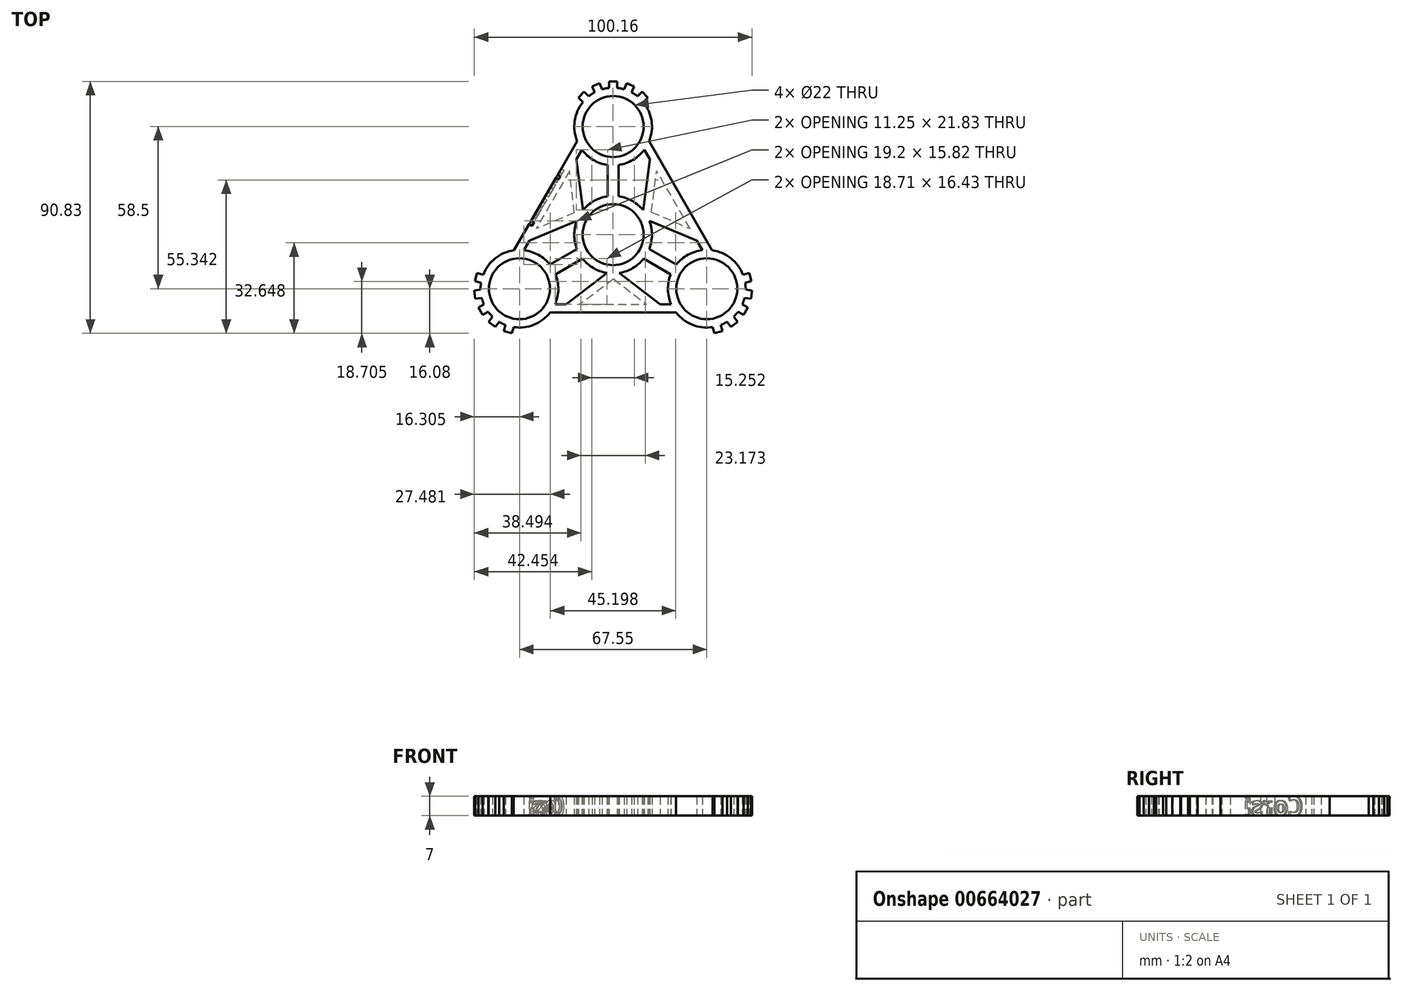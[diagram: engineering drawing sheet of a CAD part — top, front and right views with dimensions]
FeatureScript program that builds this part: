
annotation { "Feature Type Name" : "Feature", "Feature Type Description" : "" }
export const myFeature = defineFeature(function(context is Context, id is Id, definition is map)
    precondition{}
    {
        {
            var Q0;
            Q0=qCreatedBy(makeId("Top.planeOp"),FACE);
            var sketch = newSketch(context, id + "F0", { "sketchPlane" : qUnion([Q0])});
            skCircle(sketch, "E0", {"center": v(0, 0) * mm, "radius": 11 * mm});
            skArc(sketch, "E1.0", {"start": v(-2, 13.86) * mm, "mid": v(-6.9, 12.18) * mm, "end": v(-10.85, 8.84) * mm});
            skCircle(sketch, "E2", {"center": v(0, 39) * mm, "radius": 11 * mm});
            skArc(sketch, "E3.0", {"start": v(-10.9, 47.78) * mm, "mid": v(-13.85, 41.03) * mm, "end": v(-12.97, 33.72) * mm});
            skLineSegment(sketch, "E4", {"start": v(0, 11) * mm, "end": v(0, 28) * mm, "construction": true});
            skLineSegment(sketch, "E5.0", {"start": v(2, 13.86) * mm, "end": v(2, 25.14) * mm});
            skLineSegment(sketch, "E6.0", {"start": v(-2, 13.86) * mm, "end": v(-2, 25.14) * mm});
            skLineSegment(sketch, "E7", {"start": v(0, 53) * mm, "end": v(0, 55) * mm, "construction": true});
            skLineSegment(sketch, "E8.0", {"start": v(1.5, 52.92) * mm, "end": v(1.5, 55.25) * mm});
            skLineSegment(sketch, "E9.0", {"start": v(-1.5, 52.92) * mm, "end": v(-1.5, 55.25) * mm});
            skLineSegment(sketch, "E10", {"start": v(-1.5, 55.25) * mm, "end": v(1.5, 55.25) * mm});
            skLineSegment(sketch, "E11.1.0", {"start": v(4.83, 54.59) * mm, "end": v(7.6, 53.44) * mm});
            skLineSegment(sketch, "E11.1.1", {"start": v(3.94, 52.43) * mm, "end": v(4.83, 54.59) * mm});
            skLineSegment(sketch, "E11.1.2", {"start": v(6.71, 51.29) * mm, "end": v(7.6, 53.44) * mm});
            skLineSegment(sketch, "E11.2.0", {"start": v(10.43, 51.55) * mm, "end": v(12.55, 49.43) * mm});
            skLineSegment(sketch, "E11.2.1", {"start": v(8.78, 49.9) * mm, "end": v(10.43, 51.55) * mm});
            skLineSegment(sketch, "E11.2.2", {"start": v(10.9, 47.78) * mm, "end": v(12.55, 49.43) * mm});
            skLineSegment(sketch, "E11.anchor1", {"start": v(0, 39) * mm, "end": v(-1.5, 55.25) * mm, "construction": true});
            skLineSegment(sketch, "E11.anchor2", {"start": v(0, 39) * mm, "end": v(10.43, 51.55) * mm, "construction": true});
            skLineSegment(sketch, "E12.MirrorCS", {"start": v(-4.83, 54.59) * mm, "end": v(-7.6, 53.44) * mm});
            skLineSegment(sketch, "E13.MirrorCS", {"start": v(-3.94, 52.43) * mm, "end": v(-4.83, 54.59) * mm});
            skLineSegment(sketch, "E14.MirrorCS", {"start": v(-6.71, 51.29) * mm, "end": v(-7.6, 53.44) * mm});
            skLineSegment(sketch, "E15.MirrorCS", {"start": v(-8.78, 49.9) * mm, "end": v(-10.43, 51.55) * mm});
            skLineSegment(sketch, "E16.MirrorCS", {"start": v(-10.43, 51.55) * mm, "end": v(-12.55, 49.43) * mm});
            skLineSegment(sketch, "E17.MirrorCS", {"start": v(-10.9, 47.78) * mm, "end": v(-12.55, 49.43) * mm});
            skArc(sketch, "E18.trimOffspring", {"start": v(-6.71, 51.29) * mm, "mid": v(-7.78, 50.64) * mm, "end": v(-8.78, 49.9) * mm});
            skArc(sketch, "E19.trimOffspring", {"start": v(-1.29, 52.94) * mm, "mid": v(-2.63, 52.75) * mm, "end": v(-3.94, 52.43) * mm});
            skArc(sketch, "E20.trimOffspring", {"start": v(3.94, 52.43) * mm, "mid": v(2.73, 52.73) * mm, "end": v(1.5, 52.92) * mm});
            skArc(sketch, "E21.trimOffspring", {"start": v(8.95, 49.77) * mm, "mid": v(7.87, 50.58) * mm, "end": v(6.71, 51.29) * mm});
            skArc(sketch, "E22.trimOffspring", {"start": v(2, 25.14) * mm, "mid": v(7.18, 26.98) * mm, "end": v(11.26, 30.68) * mm});
            skLineSegment(sketch, "E23.1.0", {"start": v(-33.77, -19.5) * mm, "end": v(-47.1, -28.92) * mm, "construction": true});
            skPoint(sketch, "E23.1.1", {"position": v(-33.77, -19.5) * mm});
            skCircle(sketch, "E23.1.2", {"center": v(-33.77, -19.5) * mm, "radius": 11 * mm});
            skLineSegment(sketch, "E23.1.3", {"start": v(-9.53, -5.5) * mm, "end": v(-24.25, -14) * mm, "construction": true});
            skArc(sketch, "E23.1.4", {"start": v(-35.93, -33.33) * mm, "mid": v(-28.6, -32.51) * mm, "end": v(-22.72, -28.09) * mm});
            skLineSegment(sketch, "E23.1.5", {"start": v(-13, -5.2) * mm, "end": v(-22.77, -10.84) * mm});
            skLineSegment(sketch, "E23.1.6", {"start": v(-11, -8.66) * mm, "end": v(-20.77, -14.3) * mm});
            skLineSegment(sketch, "E23.1.7", {"start": v(-33.77, -19.5) * mm, "end": v(-49.86, -16.74) * mm, "construction": true});
            skArc(sketch, "E23.1.8", {"start": v(-22.77, -10.84) * mm, "mid": v(-26.96, -7.27) * mm, "end": v(-32.2, -5.59) * mm});
            skLineSegment(sketch, "E23.1.9", {"start": v(-41.06, -31.46) * mm, "end": v(-42.48, -33.3) * mm});
            skLineSegment(sketch, "E23.1.10", {"start": v(-35.93, -33.33) * mm, "end": v(-36.53, -35.58) * mm});
            skLineSegment(sketch, "E23.1.11", {"start": v(-49.86, -16.74) * mm, "end": v(-49.08, -13.85) * mm});
            skLineSegment(sketch, "E23.1.12", {"start": v(-47.77, -19.83) * mm, "end": v(-50.08, -20.13) * mm});
            skArc(sketch, "E23.1.13", {"start": v(-47.57, -17.13) * mm, "mid": v(-47.74, -18.48) * mm, "end": v(-47.77, -19.83) * mm});
            skLineSegment(sketch, "E23.1.14", {"start": v(-44.86, -31.48) * mm, "end": v(-42.48, -33.3) * mm});
            skLineSegment(sketch, "E23.1.15", {"start": v(-45.9, -26.5) * mm, "end": v(-47.63, -27.5) * mm, "construction": true});
            skLineSegment(sketch, "E23.1.16", {"start": v(-46.58, -25.16) * mm, "end": v(-48.6, -26.33) * mm});
            skLineSegment(sketch, "E23.1.17", {"start": v(-47.1, -28.92) * mm, "end": v(-48.6, -26.33) * mm});
            skLineSegment(sketch, "E23.1.18", {"start": v(-45.08, -27.76) * mm, "end": v(-47.1, -28.92) * mm});
            skLineSegment(sketch, "E23.1.19", {"start": v(-49.7, -23.1) * mm, "end": v(-50.08, -20.13) * mm});
            skLineSegment(sketch, "E23.1.20", {"start": v(-47.38, -22.8) * mm, "end": v(-49.7, -23.1) * mm});
            skArc(sketch, "E23.1.21", {"start": v(-47.38, -22.8) * mm, "mid": v(-47.03, -24) * mm, "end": v(-46.58, -25.16) * mm});
            skArc(sketch, "E23.1.22", {"start": v(-41.06, -31.46) * mm, "mid": v(-39.97, -32.06) * mm, "end": v(-38.83, -32.56) * mm});
            skLineSegment(sketch, "E23.1.23", {"start": v(-39.43, -34.8) * mm, "end": v(-36.53, -35.58) * mm});
            skLineSegment(sketch, "E23.1.24", {"start": v(-43.44, -29.63) * mm, "end": v(-44.86, -31.48) * mm});
            skLineSegment(sketch, "E23.1.25", {"start": v(-46.83, -14.45) * mm, "end": v(-49.08, -13.85) * mm});
            skArc(sketch, "E23.1.26", {"start": v(-45.2, -27.58) * mm, "mid": v(-44.37, -28.65) * mm, "end": v(-43.44, -29.63) * mm});
            skLineSegment(sketch, "E23.1.27", {"start": v(-38.83, -32.56) * mm, "end": v(-39.43, -34.8) * mm});
            skLineSegment(sketch, "E23.1.28", {"start": v(-47.6, -17.35) * mm, "end": v(-49.86, -16.74) * mm});
            skLineSegment(sketch, "E23.2.0", {"start": v(33.77, -19.5) * mm, "end": v(48.6, -26.33) * mm, "construction": true});
            skPoint(sketch, "E23.2.1", {"position": v(33.77, -19.5) * mm});
            skCircle(sketch, "E23.2.2", {"center": v(33.77, -19.5) * mm, "radius": 11 * mm});
            skLineSegment(sketch, "E23.2.3", {"start": v(9.53, -5.5) * mm, "end": v(24.25, -14) * mm, "construction": true});
            skArc(sketch, "E23.2.4", {"start": v(46.83, -14.45) * mm, "mid": v(42.46, -8.52) * mm, "end": v(35.69, -5.63) * mm});
            skLineSegment(sketch, "E23.2.5", {"start": v(11, -8.66) * mm, "end": v(20.77, -14.3) * mm});
            skLineSegment(sketch, "E23.2.6", {"start": v(13, -5.2) * mm, "end": v(22.77, -10.84) * mm});
            skLineSegment(sketch, "E23.2.7", {"start": v(33.77, -19.5) * mm, "end": v(39.43, -34.8) * mm, "construction": true});
            skArc(sketch, "E23.2.8", {"start": v(20.77, -14.3) * mm, "mid": v(19.78, -19.71) * mm, "end": v(20.94, -25.09) * mm});
            skLineSegment(sketch, "E23.2.9", {"start": v(47.77, -19.83) * mm, "end": v(50.08, -20.13) * mm});
            skLineSegment(sketch, "E23.2.10", {"start": v(46.83, -14.45) * mm, "end": v(49.08, -13.85) * mm});
            skLineSegment(sketch, "E23.2.11", {"start": v(39.43, -34.8) * mm, "end": v(36.53, -35.58) * mm});
            skLineSegment(sketch, "E23.2.12", {"start": v(41.06, -31.46) * mm, "end": v(42.48, -33.3) * mm});
            skArc(sketch, "E23.2.13", {"start": v(38.63, -32.63) * mm, "mid": v(39.87, -32.1) * mm, "end": v(41.06, -31.46) * mm});
            skLineSegment(sketch, "E23.2.14", {"start": v(49.7, -23.1) * mm, "end": v(50.08, -20.13) * mm});
            skLineSegment(sketch, "E23.2.15", {"start": v(45.9, -26.5) * mm, "end": v(47.63, -27.5) * mm, "construction": true});
            skLineSegment(sketch, "E23.2.16", {"start": v(45.08, -27.76) * mm, "end": v(47.1, -28.92) * mm});
            skLineSegment(sketch, "E23.2.17", {"start": v(48.6, -26.33) * mm, "end": v(47.1, -28.92) * mm});
            skLineSegment(sketch, "E23.2.18", {"start": v(46.58, -25.16) * mm, "end": v(48.6, -26.33) * mm});
            skLineSegment(sketch, "E23.2.19", {"start": v(44.86, -31.48) * mm, "end": v(42.48, -33.3) * mm});
            skLineSegment(sketch, "E23.2.20", {"start": v(43.44, -29.63) * mm, "end": v(44.86, -31.48) * mm});
            skArc(sketch, "E23.2.21", {"start": v(43.44, -29.63) * mm, "mid": v(44.3, -28.73) * mm, "end": v(45.08, -27.76) * mm});
            skArc(sketch, "E23.2.22", {"start": v(47.77, -19.83) * mm, "mid": v(47.75, -18.58) * mm, "end": v(47.6, -17.35) * mm});
            skLineSegment(sketch, "E23.2.23", {"start": v(49.86, -16.74) * mm, "end": v(49.08, -13.85) * mm});
            skLineSegment(sketch, "E23.2.24", {"start": v(47.38, -22.8) * mm, "end": v(49.7, -23.1) * mm});
            skLineSegment(sketch, "E23.2.25", {"start": v(35.93, -33.33) * mm, "end": v(36.53, -35.58) * mm});
            skArc(sketch, "E23.2.26", {"start": v(46.5, -25.36) * mm, "mid": v(47, -24.1) * mm, "end": v(47.38, -22.8) * mm});
            skLineSegment(sketch, "E23.2.27", {"start": v(47.6, -17.35) * mm, "end": v(49.86, -16.74) * mm});
            skLineSegment(sketch, "E23.2.28", {"start": v(38.83, -32.56) * mm, "end": v(39.43, -34.8) * mm});
            skArc(sketch, "E24.trimOffspring", {"start": v(13, -5.2) * mm, "mid": v(14, -0.12) * mm, "end": v(13.09, 4.98) * mm});
            skArc(sketch, "E25.trimOffspring", {"start": v(-11, -8.66) * mm, "mid": v(-7.1, -12.06) * mm, "end": v(-2.23, -13.82) * mm});
            skLineSegment(sketch, "E26", {"start": v(-12.97, 33.72) * mm, "end": v(-35.69, -5.63) * mm});
            skLineSegment(sketch, "E27.0", {"start": v(-11.26, 30.68) * mm, "end": v(-13.25, 27.23) * mm});
            skArc(sketch, "E28.trimOffspring", {"start": v(-11.26, 30.68) * mm, "mid": v(-7.18, 26.98) * mm, "end": v(-2, 25.14) * mm});
            skArc(sketch, "E29.trimOffspring", {"start": v(-35.69, -5.63) * mm, "mid": v(-42.46, -8.52) * mm, "end": v(-46.83, -14.45) * mm});
            skLineSegment(sketch, "E30", {"start": v(-12.12, 7) * mm, "end": v(-28.97, 0) * mm, "construction": true});
            skLineSegment(sketch, "E31", {"start": v(-12.12, 7) * mm, "end": v(-21.73, 12.54) * mm, "construction": true});
            skLineSegment(sketch, "E32.0", {"start": v(-13.98, 7.85) * mm, "end": v(-27.74, 2.14) * mm});
            skLineSegment(sketch, "E33.0", {"start": v(-13.09, 4.98) * mm, "end": v(-30.2, -2.14) * mm});
            skLineSegment(sketch, "E34.trimOffspring", {"start": v(-30.2, -2.14) * mm, "end": v(-32.2, -5.59) * mm});
            skArc(sketch, "E35.trimOffspring", {"start": v(-13.09, 4.98) * mm, "mid": v(-14, -0.12) * mm, "end": v(-13, -5.2) * mm});
            skLineSegment(sketch, "E36.MirrorCS", {"start": v(-10.85, 8.84) * mm, "end": v(-13.25, 27.23) * mm});
            skLineSegment(sketch, "E37.trimOffspring", {"start": v(-15.72, 22.95) * mm, "end": v(-27.74, 2.14) * mm});
            skPoint(sketch, "E38.orphan", {"position": v(-10.45, 9.32) * mm});
            skLineSegment(sketch, "E39.trimOffspring", {"start": v(-13.98, 7.85) * mm, "end": v(-15.72, 22.95) * mm});
            skPoint(sketch, "E40.MirrorCS.start.orphan", {"position": v(-13.3, 4.38) * mm});
            skLineSegment(sketch, "E41.1.0", {"start": v(-22.72, -28.09) * mm, "end": v(22.72, -28.09) * mm});
            skLineSegment(sketch, "E41.1.1", {"start": v(0.2, -16.04) * mm, "end": v(-12.02, -25.09) * mm});
            skLineSegment(sketch, "E41.1.2", {"start": v(0, -14) * mm, "end": v(0, -25.09) * mm, "construction": true});
            skLineSegment(sketch, "E41.1.3", {"start": v(-12.02, -25.09) * mm, "end": v(12.02, -25.09) * mm});
            skLineSegment(sketch, "E41.1.4", {"start": v(-2.23, -13.82) * mm, "end": v(-16.95, -25.09) * mm});
            skLineSegment(sketch, "E41.1.5", {"start": v(16.95, -25.09) * mm, "end": v(20.94, -25.09) * mm});
            skLineSegment(sketch, "E41.1.6", {"start": v(2.23, -13.82) * mm, "end": v(16.95, -25.09) * mm});
            skLineSegment(sketch, "E41.1.7", {"start": v(0.2, -16.04) * mm, "end": v(12.02, -25.09) * mm});
            skLineSegment(sketch, "E41.1.8", {"start": v(0, -14) * mm, "end": v(14.49, -25.09) * mm, "construction": true});
            skLineSegment(sketch, "E41.1.9", {"start": v(-20.94, -25.09) * mm, "end": v(-16.95, -25.09) * mm});
            skLineSegment(sketch, "E41.2.0", {"start": v(35.69, -5.63) * mm, "end": v(12.97, 33.72) * mm});
            skLineSegment(sketch, "E41.2.1", {"start": v(13.8, 8.18) * mm, "end": v(27.74, 2.14) * mm});
            skLineSegment(sketch, "E41.2.2", {"start": v(12.12, 7) * mm, "end": v(21.73, 12.54) * mm, "construction": true});
            skLineSegment(sketch, "E41.2.3", {"start": v(27.74, 2.14) * mm, "end": v(15.72, 22.95) * mm});
            skLineSegment(sketch, "E41.2.4", {"start": v(13.09, 4.98) * mm, "end": v(30.2, -2.14) * mm});
            skLineSegment(sketch, "E41.2.5", {"start": v(13.25, 27.23) * mm, "end": v(11.26, 30.68) * mm});
            skLineSegment(sketch, "E41.2.6", {"start": v(10.85, 8.84) * mm, "end": v(13.25, 27.23) * mm});
            skLineSegment(sketch, "E41.2.7", {"start": v(13.8, 8.18) * mm, "end": v(15.72, 22.95) * mm});
            skLineSegment(sketch, "E41.2.8", {"start": v(12.12, 7) * mm, "end": v(14.49, 25.09) * mm, "construction": true});
            skLineSegment(sketch, "E41.2.9", {"start": v(32.2, -5.59) * mm, "end": v(30.2, -2.14) * mm});
            skArc(sketch, "E42.trimOffspring", {"start": v(12.97, 33.72) * mm, "mid": v(13.85, 41.03) * mm, "end": v(10.9, 47.78) * mm});
            skArc(sketch, "E43.trimOffspring", {"start": v(32.2, -5.59) * mm, "mid": v(26.96, -7.27) * mm, "end": v(22.77, -10.84) * mm});
            skArc(sketch, "E44.trimOffspring", {"start": v(10.85, 8.84) * mm, "mid": v(6.9, 12.18) * mm, "end": v(2, 13.86) * mm});
            skArc(sketch, "E45.trimOffspring", {"start": v(2.23, -13.82) * mm, "mid": v(7.1, -12.06) * mm, "end": v(11, -8.66) * mm});
            skArc(sketch, "E46.trimOffspring", {"start": v(22.72, -28.09) * mm, "mid": v(28.6, -32.51) * mm, "end": v(35.93, -33.33) * mm});
            skArc(sketch, "E47.trimOffspring", {"start": v(-20.94, -25.09) * mm, "mid": v(-19.78, -19.71) * mm, "end": v(-20.77, -14.3) * mm});
            skSolve(sketch);
        }
        {
            var Q0;
            Q0=qSketchRegion(id+"F0",true);
            extrude(context, id + "F1", {"entities" : qUnion([Q0]), "depth" : 7 * mm});
        }
        {
            var Q0;
            Q0=makeQuery(id+"F1.opExtrude","SWEPT_FACE",FACE,{"disambiguationData":[OSD([sQuery(id+"F0.wireOp",EDGE,"E26")])]});
            var sketch = newSketch(context, id + "F2", { "sketchPlane" : qUnion([Q0])});
            skText(sketch, "E48", { "text": "Corsi", "fontName": "OpenSans-Bold.ttf"});
            const initialGuessF2  = {"E48": [-0.01185, 0, 1, 0, 0.007]};
            skSetInitialGuess(sketch, initialGuessF2);
            skSolve(sketch);
        }
        {
            var Q0;
            Q0=qSketchRegion(id+"F2",true);
            extrude(context, id + "F3", {"entities" : qUnion([Q0]), "operationType" : NewBodyOperationType.REMOVE, "oppositeDirection" : true, "depth" : 1.1 * mm, "offsetDistance" : 25 * mm});
        }
        {
            var Q0;
            Q0=makeQuery(id+"F1.opExtrude","CAP_FACE",FACE,{"disambiguationData":[OSD([sQuery(id+"F0.wireOp",EDGE,"E0"),sQuery(id+"F0.wireOp",EDGE,"E1.0"),sQuery(id+"F0.wireOp",EDGE,"E2"),sQuery(id+"F0.wireOp",EDGE,"E3.0"),sQuery(id+"F0.wireOp",EDGE,"E5.0"),sQuery(id+"F0.wireOp",EDGE,"E6.0"),sQuery(id+"F0.wireOp",EDGE,"E8.0"),sQuery(id+"F0.wireOp",EDGE,"E9.0"),sQuery(id+"F0.wireOp",EDGE,"E10"),sQuery(id+"F0.wireOp",EDGE,"E11.1.0"),sQuery(id+"F0.wireOp",EDGE,"E11.1.1"),sQuery(id+"F0.wireOp",EDGE,"E11.1.2"),sQuery(id+"F0.wireOp",EDGE,"E11.2.0"),sQuery(id+"F0.wireOp",EDGE,"E11.2.1"),sQuery(id+"F0.wireOp",EDGE,"E11.2.2"),sQuery(id+"F0.wireOp",EDGE,"E12.MirrorCS"),sQuery(id+"F0.wireOp",EDGE,"E13.MirrorCS"),sQuery(id+"F0.wireOp",EDGE,"E14.MirrorCS"),sQuery(id+"F0.wireOp",EDGE,"E15.MirrorCS"),sQuery(id+"F0.wireOp",EDGE,"E16.MirrorCS"),sQuery(id+"F0.wireOp",EDGE,"E17.MirrorCS"),sQuery(id+"F0.wireOp",EDGE,"E18.trimOffspring"),sQuery(id+"F0.wireOp",EDGE,"E19.trimOffspring"),sQuery(id+"F0.wireOp",EDGE,"E20.trimOffspring"),sQuery(id+"F0.wireOp",EDGE,"E21.trimOffspring"),sQuery(id+"F0.wireOp",EDGE,"E22.trimOffspring"),sQuery(id+"F0.wireOp",EDGE,"E23.1.2"),sQuery(id+"F0.wireOp",EDGE,"E23.1.4"),sQuery(id+"F0.wireOp",EDGE,"E23.1.5"),sQuery(id+"F0.wireOp",EDGE,"E23.1.6"),sQuery(id+"F0.wireOp",EDGE,"E23.1.8"),sQuery(id+"F0.wireOp",EDGE,"E23.1.9"),sQuery(id+"F0.wireOp",EDGE,"E23.1.10"),sQuery(id+"F0.wireOp",EDGE,"E23.1.11"),sQuery(id+"F0.wireOp",EDGE,"E23.1.12"),sQuery(id+"F0.wireOp",EDGE,"E23.1.13"),sQuery(id+"F0.wireOp",EDGE,"E23.1.14"),sQuery(id+"F0.wireOp",EDGE,"E23.1.16"),sQuery(id+"F0.wireOp",EDGE,"E23.1.17"),sQuery(id+"F0.wireOp",EDGE,"E23.1.18"),sQuery(id+"F0.wireOp",EDGE,"E23.1.19"),sQuery(id+"F0.wireOp",EDGE,"E23.1.20"),sQuery(id+"F0.wireOp",EDGE,"E23.1.21"),sQuery(id+"F0.wireOp",EDGE,"E23.1.22"),sQuery(id+"F0.wireOp",EDGE,"E23.1.23"),sQuery(id+"F0.wireOp",EDGE,"E23.1.24"),sQuery(id+"F0.wireOp",EDGE,"E23.1.25"),sQuery(id+"F0.wireOp",EDGE,"E23.1.26"),sQuery(id+"F0.wireOp",EDGE,"E23.1.27"),sQuery(id+"F0.wireOp",EDGE,"E23.1.28"),sQuery(id+"F0.wireOp",EDGE,"E23.2.2"),sQuery(id+"F0.wireOp",EDGE,"E23.2.4"),sQuery(id+"F0.wireOp",EDGE,"E23.2.5"),sQuery(id+"F0.wireOp",EDGE,"E23.2.6"),sQuery(id+"F0.wireOp",EDGE,"E23.2.8"),sQuery(id+"F0.wireOp",EDGE,"E23.2.9"),sQuery(id+"F0.wireOp",EDGE,"E23.2.10"),sQuery(id+"F0.wireOp",EDGE,"E23.2.11"),sQuery(id+"F0.wireOp",EDGE,"E23.2.12"),sQuery(id+"F0.wireOp",EDGE,"E23.2.13"),sQuery(id+"F0.wireOp",EDGE,"E23.2.14"),sQuery(id+"F0.wireOp",EDGE,"E23.2.16"),sQuery(id+"F0.wireOp",EDGE,"E23.2.17"),sQuery(id+"F0.wireOp",EDGE,"E23.2.18"),sQuery(id+"F0.wireOp",EDGE,"E23.2.19"),sQuery(id+"F0.wireOp",EDGE,"E23.2.20"),sQuery(id+"F0.wireOp",EDGE,"E23.2.21"),sQuery(id+"F0.wireOp",EDGE,"E23.2.22"),sQuery(id+"F0.wireOp",EDGE,"E23.2.23"),sQuery(id+"F0.wireOp",EDGE,"E23.2.24"),sQuery(id+"F0.wireOp",EDGE,"E23.2.25"),sQuery(id+"F0.wireOp",EDGE,"E23.2.26"),sQuery(id+"F0.wireOp",EDGE,"E23.2.27"),sQuery(id+"F0.wireOp",EDGE,"E23.2.28"),sQuery(id+"F0.wireOp",EDGE,"E24.trimOffspring"),sQuery(id+"F0.wireOp",EDGE,"E25.trimOffspring"),sQuery(id+"F0.wireOp",EDGE,"E26"),sQuery(id+"F0.wireOp",EDGE,"E27.0"),sQuery(id+"F0.wireOp",EDGE,"E28.trimOffspring"),sQuery(id+"F0.wireOp",EDGE,"E29.trimOffspring"),sQuery(id+"F0.wireOp",EDGE,"E32.0"),sQuery(id+"F0.wireOp",EDGE,"E33.0"),sQuery(id+"F0.wireOp",EDGE,"E34.trimOffspring"),sQuery(id+"F0.wireOp",EDGE,"E35.trimOffspring"),sQuery(id+"F0.wireOp",EDGE,"E36.MirrorCS"),sQuery(id+"F0.wireOp",EDGE,"E37.trimOffspring"),sQuery(id+"F0.wireOp",EDGE,"E39.trimOffspring"),sQuery(id+"F0.wireOp",EDGE,"E41.1.0"),sQuery(id+"F0.wireOp",EDGE,"E41.1.1"),sQuery(id+"F0.wireOp",EDGE,"E41.1.3"),sQuery(id+"F0.wireOp",EDGE,"E41.1.4"),sQuery(id+"F0.wireOp",EDGE,"E41.1.5"),sQuery(id+"F0.wireOp",EDGE,"E41.1.6"),sQuery(id+"F0.wireOp",EDGE,"E41.1.7"),sQuery(id+"F0.wireOp",EDGE,"E41.1.9"),sQuery(id+"F0.wireOp",EDGE,"E41.2.0"),sQuery(id+"F0.wireOp",EDGE,"E41.2.1"),sQuery(id+"F0.wireOp",EDGE,"E41.2.3"),sQuery(id+"F0.wireOp",EDGE,"E41.2.4"),sQuery(id+"F0.wireOp",EDGE,"E41.2.5"),sQuery(id+"F0.wireOp",EDGE,"E41.2.6"),sQuery(id+"F0.wireOp",EDGE,"E41.2.7"),sQuery(id+"F0.wireOp",EDGE,"E41.2.9"),sQuery(id+"F0.wireOp",EDGE,"E42.trimOffspring"),sQuery(id+"F0.wireOp",EDGE,"E43.trimOffspring"),sQuery(id+"F0.wireOp",EDGE,"E44.trimOffspring"),sQuery(id+"F0.wireOp",EDGE,"E45.trimOffspring"),sQuery(id+"F0.wireOp",EDGE,"E46.trimOffspring"),sQuery(id+"F0.wireOp",EDGE,"E47.trimOffspring")])],"isStart":false});
            var sketch = newSketch(context, id + "F4", { "sketchPlane" : qUnion([Q0])});
            skLineSegment(sketch, "E49", {"start": v(15.72, 22.95) * mm, "end": v(27.74, 2.14) * mm});
            skLineSegment(sketch, "E50", {"start": v(27.74, 2.14) * mm, "end": v(13.8, 8.18) * mm});
            skLineSegment(sketch, "E51", {"start": v(13.8, 8.18) * mm, "end": v(15.72, 22.95) * mm});
            skLineSegment(sketch, "E52", {"start": v(-15.72, 22.95) * mm, "end": v(-13.98, 7.85) * mm});
            skLineSegment(sketch, "E53", {"start": v(-13.98, 7.85) * mm, "end": v(-27.74, 2.14) * mm});
            skLineSegment(sketch, "E54", {"start": v(-27.74, 2.14) * mm, "end": v(-15.72, 22.95) * mm});
            skLineSegment(sketch, "E55", {"start": v(12.02, -25.09) * mm, "end": v(0.2, -16.04) * mm});
            skLineSegment(sketch, "E56", {"start": v(0.2, -16.04) * mm, "end": v(-11.26, -24.53) * mm});
            skLineSegment(sketch, "E57", {"start": v(-11.26, -24.53) * mm, "end": v(-12.02, -25.09) * mm});
            skLineSegment(sketch, "E58", {"start": v(-12.02, -25.09) * mm, "end": v(0.2, -16.04) * mm});
            skLineSegment(sketch, "E59", {"start": v(12.02, -25.09) * mm, "end": v(-12.02, -25.09) * mm});
            skSolve(sketch);
        }
        {
            var Q0;
            Q0=makeQuery(id+"F4.imprint","IMPRINT",FACE,{"disambiguationData":[TD([[makeQuery(id+"F4.imprint","IMPRINT",EDGE,{"derivedFrom":sQuery(id+"F4.wireOp",EDGE,"E49")}),1.0]])]});
            var Q1;
            Q1=makeQuery(id+"F4.imprint","IMPRINT",FACE,{"disambiguationData":[TD([[makeQuery(id+"F4.imprint","IMPRINT",EDGE,{"derivedFrom":sQuery(id+"F4.wireOp",EDGE,"E55")}),-1.0]])]});
            var Q2;
            Q2=makeQuery(id+"F4.imprint","IMPRINT",FACE,{"disambiguationData":[TD([[makeQuery(id+"F4.imprint","IMPRINT",EDGE,{"derivedFrom":sQuery(id+"F4.wireOp",EDGE,"E52")}),1.0]])]});
            extrude(context, id + "F5", {"entities" : qUnion([Q0, Q1, Q2]), "operationType" : NewBodyOperationType.ADD, "oppositeDirection" : true, "depth" : 6.8 * mm, "offsetDistance" : 25 * mm});
        }
    });
